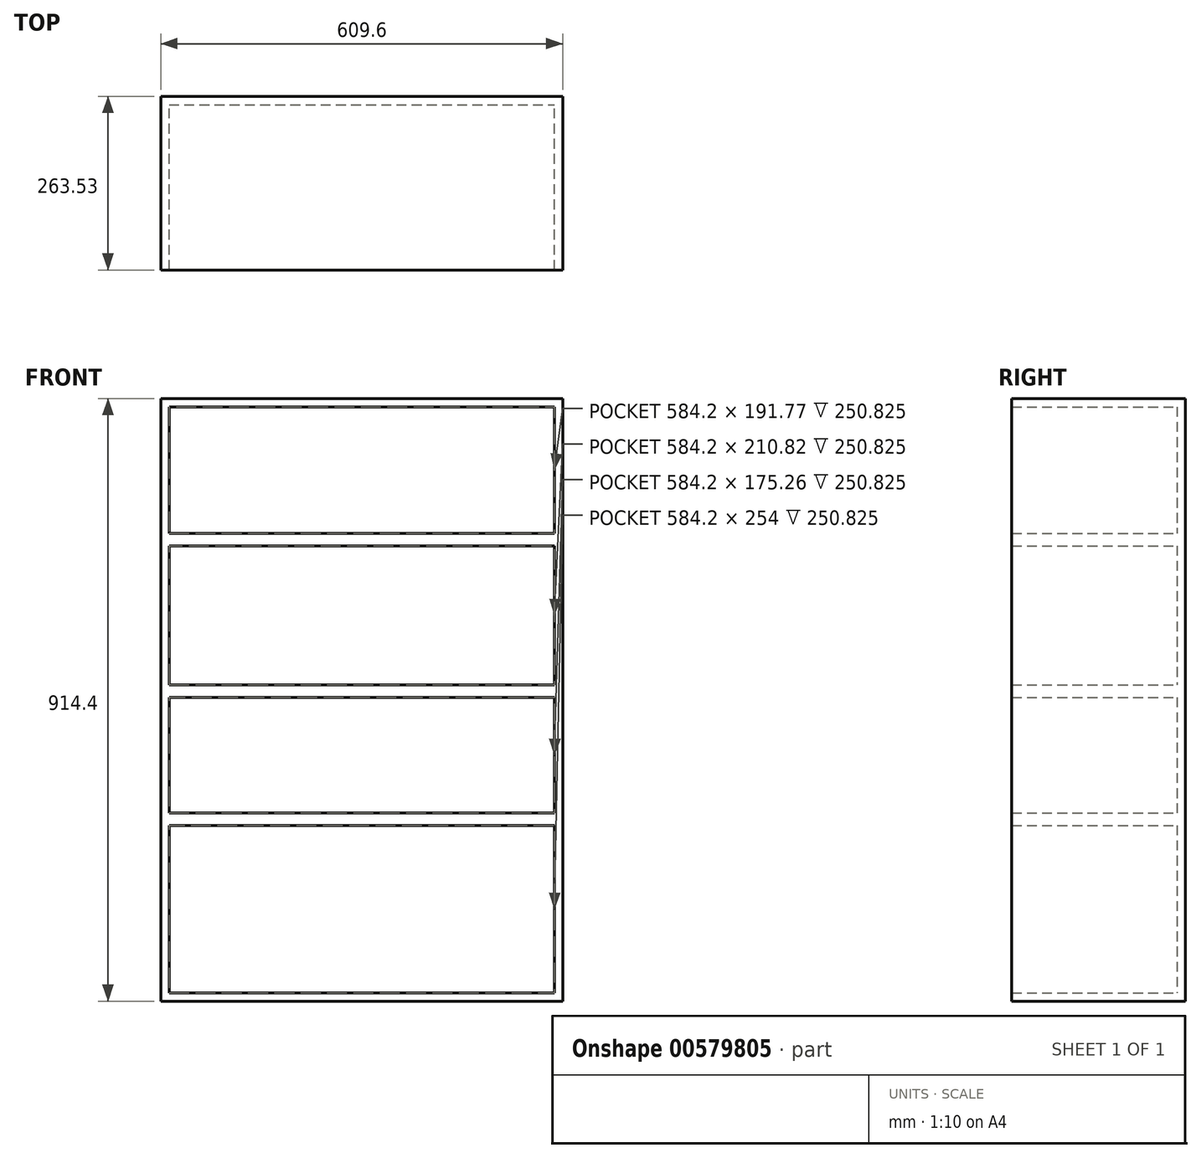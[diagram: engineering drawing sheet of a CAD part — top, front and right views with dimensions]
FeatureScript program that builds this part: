
annotation { "Feature Type Name" : "Feature", "Feature Type Description" : "" }
export const myFeature = defineFeature(function(context is Context, id is Id, definition is map)
    precondition{}
    {
        {
            var Q0;
            Q0=qCreatedBy(makeId("Front.planeOp"),FACE);
            var sketch = newSketch(context, id + "F0", { "sketchPlane" : qUnion([Q0])});
            skLineSegment(sketch, "E0.bottom", {"start": v(304.8, 457.2) * mm, "end": v(-304.8, 457.2) * mm});
            skLineSegment(sketch, "E0.top", {"start": v(304.8, -457.2) * mm, "end": v(-304.8, -457.2) * mm});
            skLineSegment(sketch, "E0.left", {"start": v(304.8, 457.2) * mm, "end": v(304.8, -457.2) * mm});
            skLineSegment(sketch, "E0.right", {"start": v(-304.8, 457.2) * mm, "end": v(-304.8, -457.2) * mm});
            skPoint(sketch, "E0.middle", {"position": v(0, 0) * mm});
            skSolve(sketch);
        }
        {
            var Q0;
            Q0=qSketchRegion(id+"F0",true);
            extrude(context, id + "F1", {"entities" : qUnion([Q0]), "depth" : 263.52 * mm, "offsetDistance" : 25.4 * mm});
        }
        {
            var Q0;
            Q0=makeQuery(id+"F1.opExtrude","CAP_FACE",FACE,{"disambiguationData":[OSD([sQuery(id+"F0.wireOp",EDGE,"E0.bottom"),sQuery(id+"F0.wireOp",EDGE,"E0.top"),sQuery(id+"F0.wireOp",EDGE,"E0.left"),sQuery(id+"F0.wireOp",EDGE,"E0.right")])],"isStart":false});
            shell(context, id + "F2", {"entities" : qUnion([Q0]), "thickness" : 12.7 * mm});
        }
        {
            var Q0;
            Q0=makeQuery(id+"F2.opShell","OFFSET_FACE",FACE,{"disambiguationData":[OSD([sQuery(id+"F0.wireOp",EDGE,"E0.bottom"),sQuery(id+"F0.wireOp",EDGE,"E0.top"),sQuery(id+"F0.wireOp",EDGE,"E0.left"),sQuery(id+"F0.wireOp",EDGE,"E0.right")])]});
            var sketch = newSketch(context, id + "F3", { "sketchPlane" : qUnion([Q0])});
            skLineSegment(sketch, "E1.bottom", {"start": v(-292.1, -190.5) * mm, "end": v(292.1, -190.5) * mm});
            skLineSegment(sketch, "E1.top", {"start": v(-292.1, -171.45) * mm, "end": v(292.1, -171.45) * mm});
            skLineSegment(sketch, "E1.left", {"start": v(-292.1, -190.5) * mm, "end": v(-292.1, -171.45) * mm});
            skLineSegment(sketch, "E1.right", {"start": v(292.1, -190.5) * mm, "end": v(292.1, -171.45) * mm});
            skPoint(sketch, "E1.middle", {"position": v(0, -180.97) * mm});
            skSolve(sketch);
        }
        {
            var Q0;
            Q0=qSketchRegion(id+"F3",true);
            extrude(context, id + "F4", {"entities" : qUnion([Q0]), "operationType" : NewBodyOperationType.ADD, "depth" : 250.82 * mm, "offsetDistance" : 25.4 * mm});
        }
        {
            var Q0;
            {var subQ0=sQuery(id+"F0.wireOp",EDGE,"E0.bottom");var subQ1=sQuery(id+"F0.wireOp",EDGE,"E0.left");var subQ2=sQuery(id+"F0.wireOp",EDGE,"E0.right");Q0=makeQuery(id+"F4.boolean.opBoolean","SPLIT",FACE,{"disambiguationData":[TD([makeQuery(id+"F2.opShell","OFFSET_FACE",FACE,{"disambiguationData":[OSD([subQ0])]})])],"derivedFrom":makeQuery(id+"F2.opShell","OFFSET_FACE",FACE,{"disambiguationData":[OSD([subQ0,sQuery(id+"F0.wireOp",EDGE,"E0.top"),subQ1,subQ2])]})});}
            var sketch = newSketch(context, id + "F5", { "sketchPlane" : qUnion([Q0])});
            skLineSegment(sketch, "E2.bottom", {"start": v(-292.1, 22.86) * mm, "end": v(292.1, 22.86) * mm});
            skLineSegment(sketch, "E2.top", {"start": v(-292.1, 3.8) * mm, "end": v(292.1, 3.8) * mm});
            skLineSegment(sketch, "E2.left", {"start": v(-292.1, 22.86) * mm, "end": v(-292.1, 3.8) * mm});
            skLineSegment(sketch, "E2.right", {"start": v(292.1, 22.86) * mm, "end": v(292.1, 3.8) * mm});
            skPoint(sketch, "E2.middle", {"position": v(0, 13.34) * mm});
            skLineSegment(sketch, "E3.bottom", {"start": v(-292.1, 252.73) * mm, "end": v(292.1, 252.73) * mm});
            skLineSegment(sketch, "E3.top", {"start": v(-292.1, 233.68) * mm, "end": v(292.1, 233.68) * mm});
            skLineSegment(sketch, "E3.left", {"start": v(-292.1, 252.73) * mm, "end": v(-292.1, 233.68) * mm});
            skLineSegment(sketch, "E3.right", {"start": v(292.1, 252.73) * mm, "end": v(292.1, 233.68) * mm});
            skPoint(sketch, "E3.middle", {"position": v(0, 243.2) * mm});
            skSolve(sketch);
        }
        {
            var Q0;
            Q0=qSketchRegion(id+"F5",true);
            extrude(context, id + "F6", {"entities" : qUnion([Q0]), "operationType" : NewBodyOperationType.ADD, "depth" : 250.82 * mm, "offsetDistance" : 25.4 * mm});
        }
        {
            var Q0;
            Q0=makeQuery(id+"F6.boolean.opBoolean","MERGE",FACE,{"derivedFrom":[makeQuery(id+"F4.boolean.opBoolean","MERGE",FACE,{"derivedFrom":[makeQuery(id+"F1.opExtrude","CAP_FACE",FACE,{"disambiguationData":[OSD([sQuery(id+"F0.wireOp",EDGE,"E0.bottom"),sQuery(id+"F0.wireOp",EDGE,"E0.top"),sQuery(id+"F0.wireOp",EDGE,"E0.left"),sQuery(id+"F0.wireOp",EDGE,"E0.right")])],"isStart":false}),makeQuery(id+"F4.opExtrude","CAP_FACE",FACE,{"disambiguationData":[OSD([sQuery(id+"F3.wireOp",EDGE,"E1.bottom"),sQuery(id+"F3.wireOp",EDGE,"E1.top"),sQuery(id+"F3.wireOp",EDGE,"E1.left"),sQuery(id+"F3.wireOp",EDGE,"E1.right")])],"isStart":false})]}),makeQuery(id+"F6.opExtrude","CAP_FACE",FACE,{"disambiguationData":[OSD([sQuery(id+"F5.wireOp",EDGE,"E2.bottom"),sQuery(id+"F5.wireOp",EDGE,"E2.top"),sQuery(id+"F5.wireOp",EDGE,"E2.left"),sQuery(id+"F5.wireOp",EDGE,"E2.right")])],"isStart":false}),makeQuery(id+"F6.opExtrude","CAP_FACE",FACE,{"disambiguationData":[OSD([sQuery(id+"F5.wireOp",EDGE,"E3.bottom"),sQuery(id+"F5.wireOp",EDGE,"E3.top"),sQuery(id+"F5.wireOp",EDGE,"E3.left"),sQuery(id+"F5.wireOp",EDGE,"E3.right")])],"isStart":false})]});
            var sketch = newSketch(context, id + "F7", { "sketchPlane" : qUnion([Q0])});
            skLineSegment(sketch, "E4", {"start": v(0, 0) * mm, "end": v(0, -171.45) * mm});
            skSolve(sketch);
        }
        {
            var Q0;
            Q0=qSketchRegion(id+"F7",true);
            var Q1;
            Q1=sQuery(id+"F7.wireOp",EDGE,"E4");
            extrude(context, id + "F8", {"entities" : qUnion([Q0]), "bodyType" : ToolBodyType.SURFACE, "surfaceEntities" : qUnion([Q1]), "oppositeDirection" : true, "depth" : 254 * mm, "offsetDistance" : 25.4 * mm});
        }
    });
